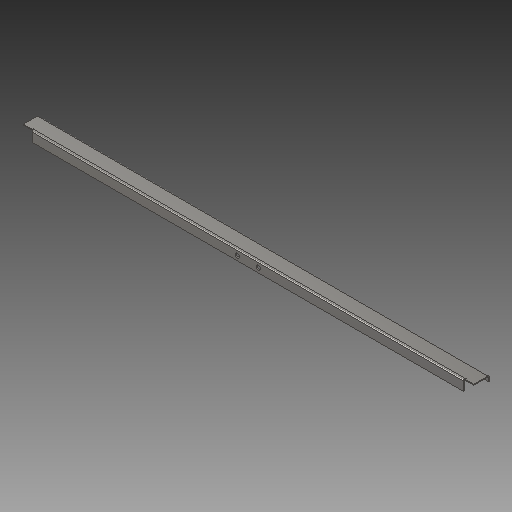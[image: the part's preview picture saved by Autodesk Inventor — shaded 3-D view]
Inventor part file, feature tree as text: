
AUTODESK INVENTOR PART (.ipt)
format: ipt  version: 2017 (Build 210142000, 142)  size: 186,368 bytes
history: native  units: mm
features: sheet_metal_op x7, other x6, sketch x4, reference x2, extrude x1, chamfer x1
ambient origin geometry x8: Origin, YZ Plane, XZ Plane, XY Plane, X Axis, Y Axis, Z Axis, Center Point
bodies: Body1 (feature_tree)
feature tree (21):
  sheet_metal_op  "Face1"
  sheet_metal_op  "Flange1"
  sheet_metal_op  "Flange2"
  extrude  "Extrusion1"  Depth=30.0mm
  chamfer  "Chamfer1"  Distance=3.0mm
  sketch  "Sketch2"  dims[d12=860.598mm d13=30.0mm]
  other  "Plate2"
  sketch  "Sketch3"  dims[d14=1.5mm]
  other  "Plate3"
  sheet_metal_op  "Bend2"
  sheet_metal_op  "Corner2"
  sketch  "Sketch4"  dims[d15=1.5mm]
  other  "Plate4"
  sheet_metal_op  "Bend3"
  sheet_metal_op  "Corner3"
  sketch  "Sketch5"  dims[d16=0.75mm d17=3.0mm d18=1.5mm d19=823.598mm d20=20.0mm d21=90.0deg d22=1.5mm d23=6.0mm d24=1.5mm d25=1.5mm d26=1.5mm d27=0.75mm d28=3.0mm d29=1.5mm d30=10.0mm d31=90.0deg d32=1.5mm d33=6.0mm d34=1.5mm d35=1.5mm d36=5.5mm d37=5.5mm d38=1.5mm d39=0.0mm d40=1.5mm d41=2.0mm d42=45.0deg]
  reference  "Reference1"
  reference  "Reference2"
  other  "Definition1"
  other  "Bancada de Lavagem Mãos - 1150 x 370 x 900h.iam"
  other  "Atrack 60 x 20 x 10:1"
